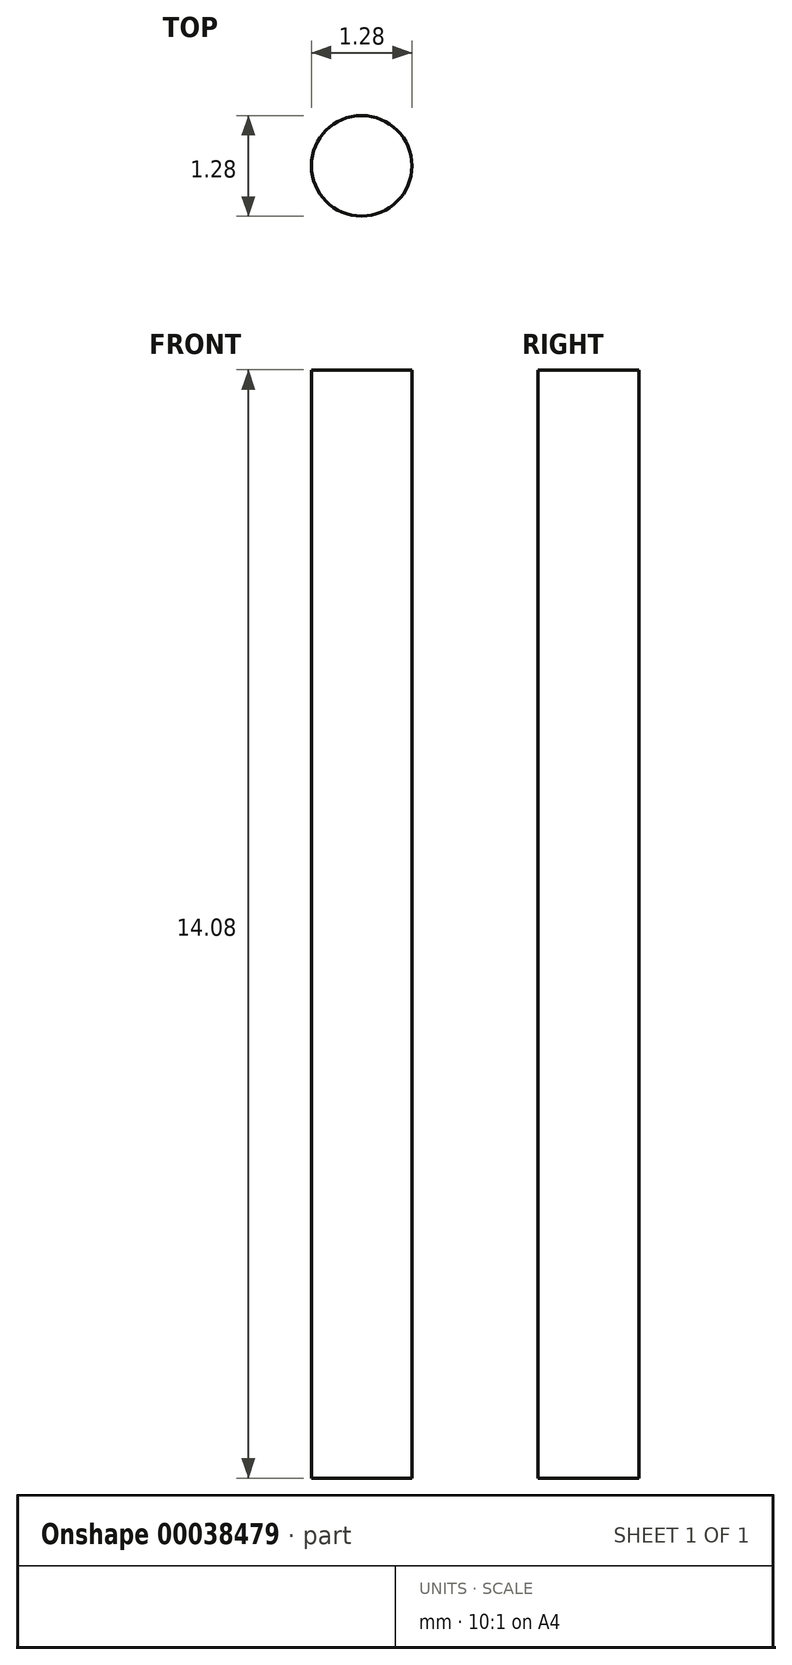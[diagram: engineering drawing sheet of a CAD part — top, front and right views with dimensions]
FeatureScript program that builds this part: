
annotation { "Feature Type Name" : "Feature", "Feature Type Description" : "" }
export const myFeature = defineFeature(function(context is Context, id is Id, definition is map)
    precondition{}
    {
        {
            var Q0;
            Q0=qCreatedBy(makeId("Front.planeOp"),FACE);
            var sketch = newSketch(context, id + "F0", { "sketchPlane" : qUnion([Q0])});
            skLineSegment(sketch, "E0.bottom", {"start": v(0, 8.07) * mm, "end": v(1.28, 8.07) * mm});
            skLineSegment(sketch, "E0.top", {"start": v(0, -6.01) * mm, "end": v(1.28, -6.01) * mm});
            skLineSegment(sketch, "E0.left", {"start": v(0, 8.07) * mm, "end": v(0, -6.01) * mm});
            skLineSegment(sketch, "E0.right", {"start": v(1.28, 8.07) * mm, "end": v(1.28, -6.01) * mm});
            skLineSegment(sketch, "E1", {"start": v(0.64, 20.52) * mm, "end": v(0.64, -15.59) * mm});
            skPoint(sketch, "E1.startSnap0", {"position": v(0.64, 8.07) * mm});
            skSolve(sketch);
        }
        {
            var Q0;
            {var subQ0=sQuery(id+"F0.wireOp",EDGE,"E0.left");Q0=makeQuery(id+"F0.imprint","IMPRINT",FACE,{"disambiguationData":[TD([[makeQuery(id+"F0.imprint","IMPRINT",EDGE,{"derivedFrom":subQ0}),1.0]])]});}
            var Q1;
            Q1=sQuery(id+"F0.wireOp",EDGE,"E1");
            revolve(context, id + "F1", {"entities" : qUnion([Q0]), "axis" : qUnion([Q1]), "revolveType" : RevolveType.FULL});
        }
    });
